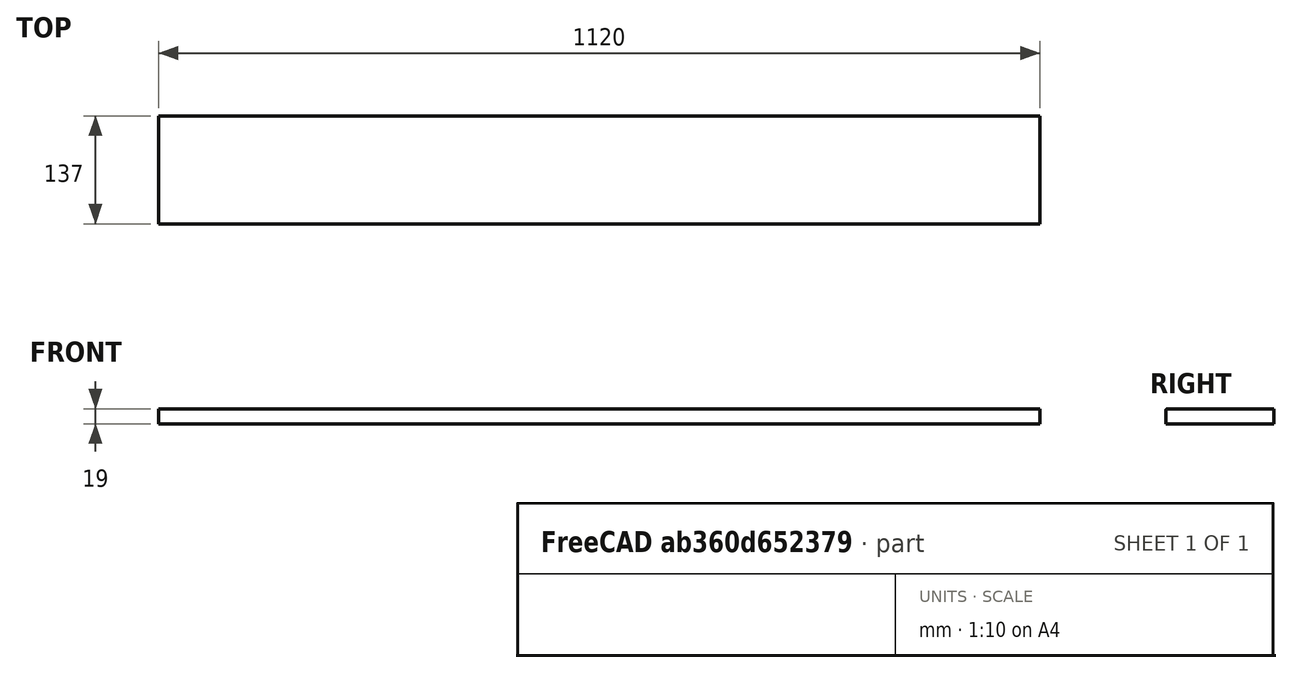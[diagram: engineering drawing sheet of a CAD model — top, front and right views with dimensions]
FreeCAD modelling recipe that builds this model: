
FCSTD DOCUMENT  (FreeCAD 0.18R14555 (Git shallow))
Label: PanneauDessusConsole
License: All rights reserved
LicenseURL: http://en.wikipedia.org/wiki/All_rights_reserved
objects: Drawing::FeatureViewPython×4, Drawing::FeatureViewPart×3, Part::Box×1, Part::Fillet×1, Drawing::FeaturePage×1
note: 2 computed .brp shape members not serialized (recipe doc carries the construction recipe); baked Part::Feature solids carry a one-line shape summary decoded from their .brp

FEATURE [Part::Box] Box  label="Cube"
  AttacherType = Attacher::AttachEngine3D
  Height = 19
  Length = 1120
  Width = 137
FEATURE [Part::Fillet] Fillet
  Base = -> Box
  Edges = 1 edges r=1: [Edge10]
FEATURE [Drawing::FeatureViewPart] Ortho  label="Ortho_0_0"
  Direction = (0,0,1)
  HiddenWidth = 0.15
  LineWidth = 0.35
  Rotation = 0
  Scale = 0.2
  ShowHiddenLines = false
  ShowSmoothLines = true
  Source = -> Fillet
  Tolerance = 0.05
  ViewResult = <g id="Ortho_0_0"\n   transform="rotate(0,26.1333,122.067) translate(26.1333,122.067) scale(0.2,0.2)"\n  >\n<g   fill="none"\n   stroke="rgb(0, 0, 0)"\n   stroke-linecap="butt"\n   stroke-linejoin="miter"\n   stroke-width="1.750000"\n   transform="scale(1,-1)"\n  >\n<path d="M0,-2.22045e-16 C0,0.00209593 0,0.00419186 0,0.00628779  C0,0.0125492 0,0.0188107 0,0.0250721  C0,0.0354203 0,0.0457685 0,0.0561167  C0,0.0704215 0,0.0847263 0,0.0990311  C0,0.117113 0,0.135194 0,0.153276  C0,0.174907 0,0.196538 0,0.218169  C0,0.243077 0,0.267985 0,0.292893  C0,0.320766 0,0.348638 0,0.37651  C0,0.436231 0,0.499433 0,0.566116  C0,0.701837 0,0.850207 0,1 " /><path id= "2" d=" M 0 1 L 0 137 " />\n<path id= "3" d=" M 0 -2.22045e-16 L 1120 -2.22045e-16 " />\n<path d="M1120,-2.22045e-16 C1120,0.00209593 1120,0.00419186 1120,0.00628779  C1120,0.0125492 1120,0.0188107 1120,0.0250721  C1120,0.0354203 1120,0.0457685 1120,0.0561167  C1120,0.0704215 1120,0.0847263 1120,0.0990311  C1120,0.117113 1120,0.135194 1120,0.153276  C1120,0.174907 1120,0.196538 1120,0.218169  C1120,0.243077 1120,0.267985 1120,0.292893  C1120,0.320766 1120,0.348638 1120,0.37651  C1120,0.436231 1120,0.499433 1120,0.566116  C1120,0.701837 1120,0.850207 1120,1 " /><path id= "5" d=" M 0 137 L 1120 137 " />\n<path id= "6" d=" M 1120 1 L 1120 137 " />\n</g>\n<g   fill="none"\n   stroke="rgb(0, 0, 0)"\n   stroke-linecap="butt"\n   stroke-linejoin="miter"\n   stroke-width="1.750000"\n   transform="scale(1,-1)"\n  >\n<path id= "1" d=" M 0 1 L 1120 1 " />\n</g>\n</g>
  Visible = false
  X = 26.1333
  Y = 122.067
FEATURE [Drawing::FeatureViewPart] Ortho001  label="Ortho_1_0"
  Direction = (-1,0,0)
  HiddenWidth = 0.15
  LineWidth = 0.35
  Rotation = 180
  Scale = 0.2
  ShowHiddenLines = false
  ShowSmoothLines = true
  Source = -> Fillet
  Tolerance = 0.05
  ViewResult = <g id="Ortho_1_0"\n   transform="rotate(180,266.267,122.067) translate(266.267,122.067) scale(0.2,0.2)"\n  >\n<g   fill="none"\n   stroke="rgb(0, 0, 0)"\n   stroke-linecap="butt"\n   stroke-linejoin="miter"\n   stroke-width="1.750000"\n   transform="scale(1,-1)"\n  >\n<path id= "1" d=" M 0 0 L -18 0 " />\n<path d="M-18 2.22045e-16 A1 1 0 0 1 -19 -1" /><path id= "3" d=" M 0 0 L 0 -137 " />\n<path id= "4" d=" M -19 -1 L -19 -137 " />\n<path id= "5" d=" M 0 -137 L -19 -137 " />\n</g>\n</g>
  Visible = false
  X = 266.267
  Y = 122.067
FEATURE [Drawing::FeatureViewPart] Ortho002  label="Ortho_0_1"
  Direction = (0,-1,0)
  HiddenWidth = 0.15
  LineWidth = 0.35
  Rotation = 90
  Scale = 0.2
  ShowHiddenLines = false
  ShowSmoothLines = true
  Source = -> Fillet
  Tolerance = 0.05
  ViewResult = <g id="Ortho_0_1"\n   transform="rotate(90,26.1333,54.5333) translate(26.1333,54.5333) scale(0.2,0.2)"\n  >\n<g   fill="none"\n   stroke="rgb(0, 0, 0)"\n   stroke-linecap="butt"\n   stroke-linejoin="miter"\n   stroke-width="1.750000"\n   transform="scale(1,-1)"\n  >\n<path id= "1" d=" M 0 0 L -18 0 " />\n<path d="M-18,0 Q-18.1694,0 -18.3303,0  Q-18.4354,0 -18.532,0  Q-18.6257,0 -18.7071,0  Q-18.7445,0 -18.7818,0  Q-18.8143,0 -18.8467,0  Q-18.8738,0 -18.901,0  Q-18.9224,0 -18.9439,0  Q-18.9594,0 -18.9749,0  Q-18.9843,0 -18.9937,0  Q-18.9969,0 -19,0 " /><path id= "3" d=" M 0 1120 L -18 1120 " />\n<path id= "4" d=" M 0 0 L 0 1120 " />\n<path id= "5" d=" M -19 0 L -19 1120 " />\n<path d="M-18,1120 Q-18.1694,1120 -18.3303,1120  Q-18.4354,1120 -18.532,1120  Q-18.6257,1120 -18.7071,1120  Q-18.7445,1120 -18.7818,1120  Q-18.8143,1120 -18.8467,1120  Q-18.8738,1120 -18.901,1120  Q-18.9224,1120 -18.9439,1120  Q-18.9594,1120 -18.9749,1120  Q-18.9843,1120 -18.9937,1120  Q-18.9969,1120 -19,1120 " /></g>\n<g   fill="none"\n   stroke="rgb(0, 0, 0)"\n   stroke-linecap="butt"\n   stroke-linejoin="miter"\n   stroke-width="1.750000"\n   transform="scale(1,-1)"\n  >\n<path id= "1" d=" M -18 0 L -18 1120 " />\n</g>\n</g>
  Visible = false
  X = 26.1333
  Y = 54.5333
FEATURE [Drawing::FeatureViewPython] dim001  # drawing view (typed FeaturePython)
  Rotation = 0
  ViewResult = <g> \n  <line x1="26.133300" y1="92.667000" x2="26.133300" y2="79.304833" style="stroke:rgb(0,0,255);stroke-width:0.30" />\n<line x1="250.133300" y1="92.667000" x2="250.133300" y2="79.304833" style="stroke:rgb(0,0,255);stroke-width:0.30" />\n<line x1="26.133300" y1="80.304833" x2="250.133300" y2="80.304833" style="stroke:rgb(0,0,255);stroke-width:0.30" /> \n  <polygon points="250.133300,80.304833 247.133300,79.304833 246.133300,80.304833 247.133300,81.304833" style="fill:rgb(0,0,255);stroke:rgb(0,0,255);stroke-width:0" /><polygon points="26.133300,80.304833 29.133300,81.304833 30.133300,80.304833 29.133300,79.304833" style="fill:rgb(0,0,255);stroke:rgb(0,0,255);stroke-width:0" /> \n  <text x="138.133300" y="78.304833" font-family="Verdana" font-size="3.6" fill="rgb(0,0,255)" text-anchor="middle" transform="rotate(0.000000 138.133300,78.304833)" >1120</text> </g>
  Visible = true
  X = 0
  Y = 0
  arrowL1 = 3
  arrowL2 = 1
  arrowW = 2
  arrow_scheme = 0
  autoPlaceOffset = 2
  autoPlaceText = true
  click1_x = 145
  click1_y = 80.3048
  click2_x = 145
  click2_y = 80.3048
  comma_decimal_place = false
  dimension_line_overshoot = 1
  gap_datum_points = 2
  halfDimension_linear = false
  lineColor = rgb(0,0,255)
  strokeWidth = 0.3
  textFormat_linear = %(value)3.0f
  textRenderer_color = rgb(0,0,255)
  textRenderer_family = Verdana
  textRenderer_size = 3.6
  unit_custom_scale = 1
  unit_scheme = 0
FEATURE [Drawing::FeatureViewPython] dim002  # drawing view (typed FeaturePython)
  Rotation = 0
  ViewResult = <g> \n  <line x1="24.133300" y1="122.047194" x2="19.000000" y2="122.047194" style="stroke:rgb(0,0,255);stroke-width:0.30" />\n<line x1="24.133300" y1="94.667000" x2="19.000000" y2="94.667000" style="stroke:rgb(0,0,255);stroke-width:0.30" />\n<line x1="20.000000" y1="122.047194" x2="20.000000" y2="94.667000" style="stroke:rgb(0,0,255);stroke-width:0.30" /> \n  <polygon points="20.000000,94.667000 19.000000,97.667000 20.000000,98.667000 21.000000,97.667000" style="fill:rgb(0,0,255);stroke:rgb(0,0,255);stroke-width:0" /><polygon points="20.000000,122.047194 21.000000,119.047194 20.000000,118.047194 19.000000,119.047194" style="fill:rgb(0,0,255);stroke:rgb(0,0,255);stroke-width:0" /> \n  <text x="18.000000" y="108.357097" font-family="Verdana" font-size="3.6" fill="rgb(0,0,255)" text-anchor="middle" transform="rotate(-90.000000 18.000000,108.357097)" >137</text> </g>
  Visible = true
  X = 0
  Y = 0
  arrowL1 = 3
  arrowL2 = 1
  arrowW = 2
  arrow_scheme = 0
  autoPlaceOffset = 2
  autoPlaceText = true
  click1_x = 20
  click1_y = 90.2324
  click2_x = 20
  click2_y = 90.2324
  comma_decimal_place = false
  dimension_line_overshoot = 1
  gap_datum_points = 2
  halfDimension_linear = false
  lineColor = rgb(0,0,255)
  strokeWidth = 0.3
  textFormat_linear = %(value)3.0f
  textRenderer_color = rgb(0,0,255)
  textRenderer_family = Verdana
  textRenderer_size = 3.6
  unit_custom_scale = 1
  unit_scheme = 0
FEATURE [Drawing::FeatureViewPython] dim003  # drawing view (typed FeaturePython)
  Rotation = 0
  ViewResult = <g> \n  <line x1="24.133300" y1="50.733300" x2="19.000000" y2="50.733300" style="stroke:rgb(0,0,255);stroke-width:0.30" />\n<line x1="24.133300" y1="54.533300" x2="19.000000" y2="54.533300" style="stroke:rgb(0,0,255);stroke-width:0.30" />\n<line x1="20.000000" y1="50.733300" x2="20.000000" y2="54.533300" style="stroke:rgb(0,0,255);stroke-width:0.30" /> \n  <polygon points="20.000000,54.533300 19.000000,57.533300 20.000000,58.533300 21.000000,57.533300" style="fill:rgb(0,0,255);stroke:rgb(0,0,255);stroke-width:0" /><polygon points="20.000000,50.733300 21.000000,47.733300 20.000000,46.733300 19.000000,47.733300" style="fill:rgb(0,0,255);stroke:rgb(0,0,255);stroke-width:0" /> \n  <text x="18.000000" y="52.633300" font-family="Verdana" font-size="3.6" fill="rgb(0,0,255)" text-anchor="middle" transform="rotate(-90.000000 18.000000,52.633300)" > 19</text> </g>
  Visible = true
  X = 0
  Y = 0
  arrowL1 = 3
  arrowL2 = 1
  arrowW = 2
  arrow_scheme = 0
  autoPlaceOffset = 2
  autoPlaceText = true
  click1_x = 20
  click1_y = 50.7884
  click2_x = 20
  click2_y = 50.7884
  comma_decimal_place = false
  dimension_line_overshoot = 1
  gap_datum_points = 2
  halfDimension_linear = false
  lineColor = rgb(0,0,255)
  strokeWidth = 0.3
  textFormat_linear = %(value)3.0f
  textRenderer_color = rgb(0,0,255)
  textRenderer_family = Verdana
  textRenderer_size = 3.6
  unit_custom_scale = 1
  unit_scheme = 0
FEATURE [Drawing::FeatureViewPython] noteCircle001  # drawing view (typed FeaturePython)
  Rotation = 0
  ViewResult = <g> <line x1="125.000000" y1="139.870051" x2="138.133300" y2="121.867000" style="stroke:rgb(0,0,255);stroke-width:0.30" />\n<line x1="125.000000" y1="139.870051" x2="140.000000" y2="139.870051" style="stroke:rgb(0,0,255);stroke-width:0.30" />\n <circle cx ="140.000000" cy ="139.870051" r="4.500000" stroke="rgb(0,0,255)" fill="rgb(255,255,255)" /> \n<text x="138.500000" y="141.370051" font-family="inherit" font-size="5" fill="rgb(0,150,0)" text-anchor="inherit"  >1</text> </g>
  Visible = true
  X = 0
  Y = 0
  click1_x = 125
  click1_y = 139.87
  click2_x = 140
  click2_y = 139.87
  lineColor = rgb(0,0,255)
  noteCircle_fill = rgb(255,255,255)
  noteCircle_radius = 4.5
  noteText = 1
  strokeWidth = 0.3
  textRenderer_noteCircle_color = rgb(0,150,0)
  textRenderer_noteCircle_family = inherit
  textRenderer_noteCircle_size = 5
FEATURE [Drawing::FeaturePage] Page
  EditableTexts = GB | Panneau dessus | 1 : congé rayon 1mm | A4 | X / Y | 2/10 | PN | DN | DD/MM/YYYY | REV A
  Group = -> [Ortho,Ortho001,Ortho002,dim001,dim002,dim003,noteCircle001]
  Template = /app/freecad/data/Mod/Drawing/Templates/A4_Landscape_ISO7200.svg
